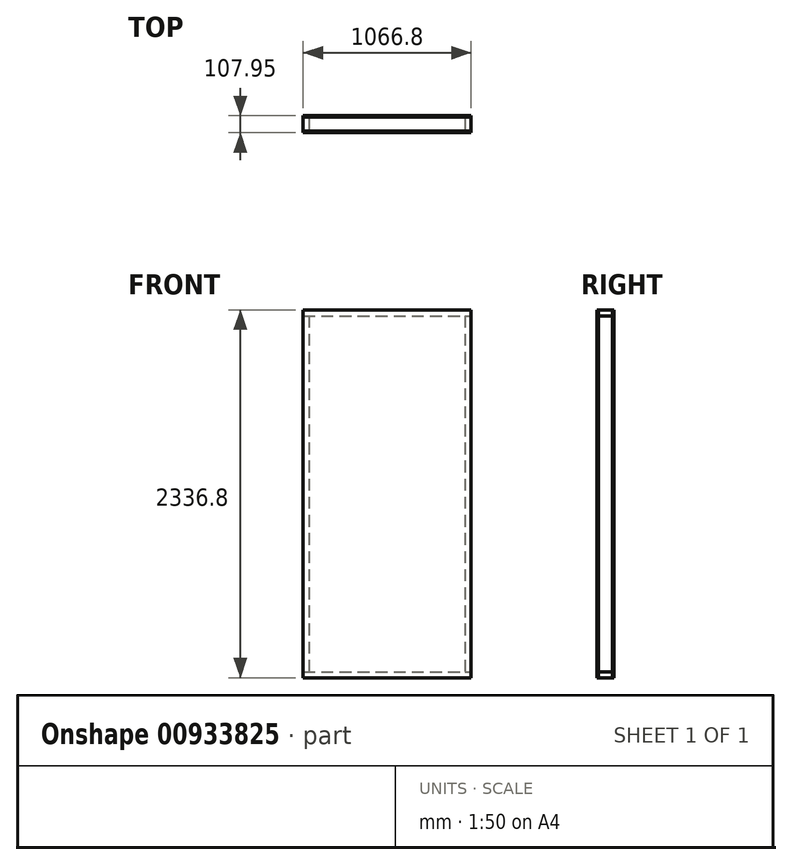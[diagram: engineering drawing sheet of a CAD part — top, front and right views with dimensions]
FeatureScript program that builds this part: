
annotation { "Feature Type Name" : "Feature", "Feature Type Description" : "" }
export const myFeature = defineFeature(function(context is Context, id is Id, definition is map)
    precondition{}
    {
        {
            var Q0;
            Q0=qCreatedBy(makeId("Top.planeOp"),FACE);
            var sketch = newSketch(context, id + "F0", { "sketchPlane" : qUnion([Q0])});
            skLineSegment(sketch, "E0.bottom", {"start": v(-50.87, 64.8) * mm, "end": v(1015.93, 64.8) * mm});
            skLineSegment(sketch, "E0.top", {"start": v(-50.87, -24.1) * mm, "end": v(1015.93, -24.1) * mm});
            skLineSegment(sketch, "E0.left", {"start": v(-50.87, 64.8) * mm, "end": v(-50.87, -24.1) * mm});
            skLineSegment(sketch, "E0.right", {"start": v(1015.93, 64.8) * mm, "end": v(1015.93, -24.1) * mm});
            skSolve(sketch);
        }
        {
            var Q0;
            Q0=makeQuery(id+"F0.imprint","IMPRINT",FACE,{"disambiguationData":[TD([[makeQuery(id+"F0.imprint","IMPRINT",EDGE,{"derivedFrom":sQuery(id+"F0.wireOp",EDGE,"E0.bottom")}),-1.0]])]});
            extrude(context, id + "F1", {"entities" : qUnion([Q0]), "depth" : 38.1 * mm, "offsetDistance" : 25.4 * mm});
        }
        {
            var Q0;
            Q0=makeQuery(id+"F1.opExtrude","CAP_FACE",FACE,{"disambiguationData":[OSD([sQuery(id+"F0.wireOp",EDGE,"E0.bottom"),sQuery(id+"F0.wireOp",EDGE,"E0.top"),sQuery(id+"F0.wireOp",EDGE,"E0.left"),sQuery(id+"F0.wireOp",EDGE,"E0.right")])],"isStart":false});
            var sketch = newSketch(context, id + "F2", { "sketchPlane" : qUnion([Q0])});
            skLineSegment(sketch, "E1.bottom", {"start": v(-50.87, 64.8) * mm, "end": v(-12.77, 64.8) * mm});
            skLineSegment(sketch, "E1.top", {"start": v(-50.87, -24.1) * mm, "end": v(-12.77, -24.1) * mm});
            skLineSegment(sketch, "E1.left", {"start": v(-50.87, 64.8) * mm, "end": v(-50.87, -24.1) * mm});
            skLineSegment(sketch, "E1.right", {"start": v(-12.77, 64.8) * mm, "end": v(-12.77, -24.1) * mm});
            skLineSegment(sketch, "E2.bottom", {"start": v(1015.93, 64.8) * mm, "end": v(977.83, 64.8) * mm});
            skLineSegment(sketch, "E2.top", {"start": v(1015.93, -24.1) * mm, "end": v(977.83, -24.1) * mm});
            skLineSegment(sketch, "E2.left", {"start": v(1015.93, 64.8) * mm, "end": v(1015.93, -24.1) * mm});
            skLineSegment(sketch, "E2.right", {"start": v(977.83, 64.8) * mm, "end": v(977.83, -24.1) * mm});
            skSolve(sketch);
        }
        {
            var Q0;
            Q0=makeQuery(id+"F2.imprint","IMPRINT",FACE,{"disambiguationData":[TD([[makeQuery(id+"F2.imprint","IMPRINT",EDGE,{"derivedFrom":sQuery(id+"F2.wireOp",EDGE,"E1.bottom")}),-1.0]])]});
            var Q1;
            Q1=makeQuery(id+"F2.imprint","IMPRINT",FACE,{"disambiguationData":[TD([[makeQuery(id+"F2.imprint","IMPRINT",EDGE,{"derivedFrom":sQuery(id+"F2.wireOp",EDGE,"E2.bottom")}),-1.0]])]});
            extrude(context, id + "F3", {"entities" : qUnion([Q0, Q1]), "depth" : 2260.6 * mm, "offsetDistance" : 25.4 * mm});
        }
        {
            var Q0;
            Q0=makeQuery(id+"F3.opExtrude","CAP_FACE",FACE,{"disambiguationData":[OSD([sQuery(id+"F2.wireOp",EDGE,"E1.bottom"),sQuery(id+"F2.wireOp",EDGE,"E1.top"),sQuery(id+"F2.wireOp",EDGE,"E1.left"),sQuery(id+"F2.wireOp",EDGE,"E1.right")])],"isStart":false});
            var sketch = newSketch(context, id + "F4", { "sketchPlane" : qUnion([Q0])});
            skLineSegment(sketch, "E3.bottom", {"start": v(-50.87, 64.8) * mm, "end": v(1015.93, 64.8) * mm});
            skLineSegment(sketch, "E3.top", {"start": v(-50.87, -24.1) * mm, "end": v(1015.93, -24.1) * mm});
            skLineSegment(sketch, "E3.left", {"start": v(-50.87, 64.8) * mm, "end": v(-50.87, -24.1) * mm});
            skLineSegment(sketch, "E3.right", {"start": v(1015.93, 64.8) * mm, "end": v(1015.93, -24.1) * mm});
            skSolve(sketch);
        }
        {
            var Q0;
            {var subQ0=sQuery(id+"F4.wireOp",EDGE,"E3.left");Q0=makeQuery(id+"F4.imprint","IMPRINT",FACE,{"disambiguationData":[TD([[makeQuery(id+"F4.imprint","IMPRINT",EDGE,{"derivedFrom":subQ0}),1.0]])]});}
            var Q1;
            {var subQ2=sQuery(id+"F4.wireOp",EDGE,"E3.right");Q1=makeQuery(id+"F4.imprint","IMPRINT",FACE,{"disambiguationData":[TD([[makeQuery(id+"F4.imprint","IMPRINT",EDGE,{"derivedFrom":subQ2}),-1.0]])]});}
            extrude(context, id + "F5", {"entities" : qUnion([Q0, Q1]), "depth" : 38.1 * mm, "offsetDistance" : 25.4 * mm});
        }
        {
            var Q0;
            Q0=makeQuery(id+"F5.opExtrude","SWEPT_FACE",FACE,{"disambiguationData":[OSD([sQuery(id+"F4.wireOp",EDGE,"E3.top")])]});
            var sketch = newSketch(context, id + "F6", { "sketchPlane" : qUnion([Q0])});
            skLineSegment(sketch, "E4.bottom", {"start": v(-50.87, 2336.8) * mm, "end": v(1015.93, 2336.8) * mm});
            skLineSegment(sketch, "E4.top", {"start": v(-50.87, 0) * mm, "end": v(1015.93, 0) * mm});
            skLineSegment(sketch, "E4.left", {"start": v(-50.87, 2336.8) * mm, "end": v(-50.87, 0) * mm});
            skLineSegment(sketch, "E4.right", {"start": v(1015.93, 2336.8) * mm, "end": v(1015.93, 0) * mm});
            skSolve(sketch);
        }
        {
            var Q0;
            Q0 = qSketchRegion(id + "F6", true);
            extrude(context, id + "F7", {"entities" : qUnion([Q0]), "depth" : 9.52 * mm, "offsetDistance" : 25.4 * mm});
        }
        {
            var Q0;
            Q0=makeQuery(id+"F5.opExtrude","CAP_EDGE",EDGE,{"disambiguationData":[OSD([sQuery(id+"F4.wireOp",EDGE,"E3.left")])],"isStart":false});
            cPoint(context, id + "F8", {"entities" : qUnion([Q0]), "parameter" : 0.5});
        }
        {
            var Q0;
            Q0=makeQuery(id+"F3.opExtrude","CAP_EDGE",EDGE,{"disambiguationData":[OSD([sQuery(id+"F2.wireOp",EDGE,"E1.left")])],"isStart":false});
            cPoint(context, id + "F9", {"entities" : qUnion([Q0]), "parameter" : 0.5});
        }
        {
            var Q0;
            Q0=makeQuery(id+"F1.opExtrude","CAP_EDGE",EDGE,{"disambiguationData":[OSD([sQuery(id+"F0.wireOp",EDGE,"E0.right")])],"isStart":true});
            cPoint(context, id + "F10", {"entities" : qUnion([Q0]), "parameter" : 0.5});
        }
        {
            var Q0;
            Q0 = qCreatedBy(id + "F8" ,VERTEX);
            var Q1;
            Q1 = qCreatedBy(id + "F9" ,VERTEX);
            var Q2;
            Q2 = qCreatedBy(id + "F10" ,VERTEX);
            cPlane(context, id + "F11", {"entities" : qUnion([Q0, Q1, Q2]), "cplaneType" : CPlaneType.THREE_POINT, "offset" : 25.4 * mm, "width" : 152.4 * mm, "height" : 152.4 * mm});
        }
        {
            var Q0;
            Q0=makeQuery(id+"F7.opExtrude","SWEPT_BODY",BODY,{"disambiguationData":[OSD([sQuery(id+"F6.wireOp",EDGE,"E4.bottom"),sQuery(id+"F6.wireOp",EDGE,"E4.top"),sQuery(id+"F6.wireOp",EDGE,"E4.left"),sQuery(id+"F6.wireOp",EDGE,"E4.right")])]});
            var Q1;
            Q1=qCreatedBy(id+"F11.planeOp",FACE);
            mirror(context, id + "F12", {"entities" : qUnion([Q0]), "mirrorPlane" : qUnion([Q1])});
        }
    });
